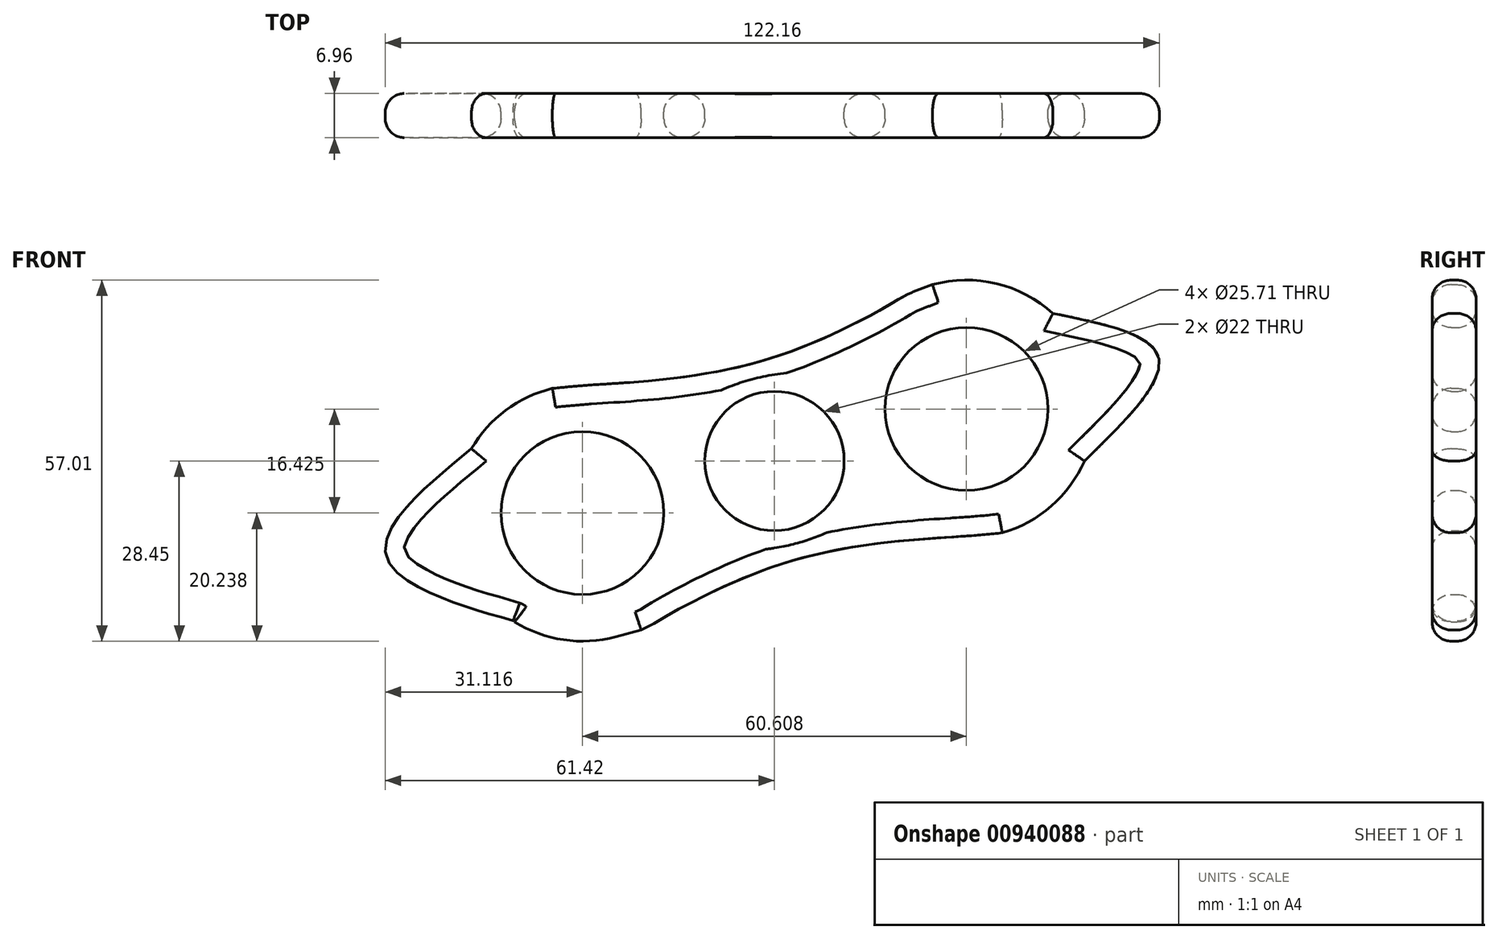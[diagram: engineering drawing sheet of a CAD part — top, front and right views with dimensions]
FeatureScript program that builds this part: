
annotation { "Feature Type Name" : "Feature", "Feature Type Description" : "" }
export const myFeature = defineFeature(function(context is Context, id is Id, definition is map)
    precondition{}
    {
        {
            var Q0;
            Q0=qCreatedBy(makeId("Front.planeOp"),FACE);
            var sketch = newSketch(context, id + "F0", { "sketchPlane" : qUnion([Q0])});
            skCircle(sketch, "E0", {"center": v(0, 0) * mm, "radius": 11 * mm});
            skPoint(sketch, "E1.0.midPoint", {"position": v(38.52, -22.1) * mm});
            skLineSegment(sketch, "E2", {"start": v(10.62, 2.88) * mm, "end": v(10.66, 2.89) * mm});
            skLineSegment(sketch, "E3", {"start": v(-10.62, -2.88) * mm, "end": v(-10.77, -2.92) * mm});
            skCircle(sketch, "E4", {"center": v(30.3, 8.21) * mm, "radius": 12.86 * mm});
            skCircle(sketch, "E5", {"center": v(-30.3, -8.21) * mm, "radius": 12.86 * mm});
            skArc(sketch, "E6", {"start": v(-42.6, -24.29) * mm, "mid": v(-34.23, -28.07) * mm, "end": v(-25.04, -27.75) * mm});
            skArc(sketch, "E7", {"start": v(43.95, 23.3) * mm, "mid": v(32.98, 28.38) * mm, "end": v(21.06, 26.34) * mm});
            skLineSegment(sketch, "E8", {"start": v(35.96, -11.34) * mm, "end": v(35.23, -11.53) * mm});
            skFitSpline(sketch, "E9", {"points": [v(-35.04, 11.46) * mm, v(-29.1, 11.99) * mm, v(-1.76, 15.86) * mm, v(19.32, 25.34) * mm, v(21.06, 26.34) * mm, v(24.94, 27.84) * mm], "startDerivative": vector(31.45, 3.25) * mm, "endDerivative": vector(35.22, 13.02) * mm});
            skFitSpline(sketch, "E10", {"points": [v(35.96, -11.34) * mm, v(30.02, -11.87) * mm, v(2.68, -15.78) * mm, v(-18.39, -25.29) * mm, v(-20.13, -26.29) * mm, v(-24, -27.8) * mm], "startDerivative": vector(-31.44, -3.3) * mm, "endDerivative": vector(-35.2, -13.06) * mm});
            skPoint(sketch, "E11.orphan", {"position": v(-16.42, 60.6) * mm});
            skPoint(sketch, "E12.orphan", {"position": v(16.42, -60.6) * mm});
            skPoint(sketch, "E13.orphan", {"position": v(60.6, 16.42) * mm});
            skLineSegment(sketch, "E14.trimOffspring", {"start": v(-21.04, -26.68) * mm, "end": v(-25.04, -27.75) * mm});
            skPoint(sketch, "E15.orphan", {"position": v(-60.6, -16.42) * mm});
            skLineSegment(sketch, "E16.trimOffspring", {"start": v(-30.05, -8.14) * mm, "end": v(-30.3, -8.21) * mm});
            skLineSegment(sketch, "E17.trimOffspring", {"start": v(30.3, 8.21) * mm, "end": v(30.45, 8.25) * mm});
            skLineSegment(sketch, "E18", {"start": v(-30.3, -8.21) * mm, "end": v(-30.05, -8.14) * mm});
            skLineSegment(sketch, "E19", {"start": v(-48.8, 0) * mm, "end": v(-48.8, 0) * mm});
            skFitSpline(sketch, "E20", {"points": [v(43.95, 23.3) * mm, v(60.6, 16.42) * mm, v(48.92, 0) * mm], "startDerivative": vector(48.13, -9.83) * mm, "endDerivative": vector(-37.39, -36.53) * mm});
            skArc(sketch, "E21.trimOffspring", {"start": v(-29.1, 11.99) * mm, "mid": v(-39.88, 9.61) * mm, "end": v(-47.81, 1.93) * mm});
            skLineSegment(sketch, "E22.trimOffspring", {"start": v(-10.77, -2.92) * mm, "end": v(-10.62, -2.88) * mm});
            skArc(sketch, "E23.trimOffspring", {"start": v(27.98, -12) * mm, "mid": v(40.42, -9.44) * mm, "end": v(48.92, 0) * mm});
            skFitSpline(sketch, "E24", {"points": [v(-47.81, 1.93) * mm, v(-60.6, -16.42) * mm, v(-41.26, -25.23) * mm, v(-41.02, -25.38) * mm], "startDerivative": vector(-50.87, -41.8) * mm, "endDerivative": vector(1.15, -2.34) * mm});
            skSolve(sketch);
        }
        {
            var Q0;
            Q0=makeQuery(id+"F0.imprint","IMPRINT",FACE,{"disambiguationData":[TD([[makeQuery(id+"F0.imprint","IMPRINT",EDGE,{"derivedFrom":sQuery(id+"F0.wireOp",EDGE,"E4")}),-1.0]])]});
            extrude(context, id + "F1", {"entities" : qUnion([Q0]), "depth" : 6.96 * mm, "offsetDistance" : 25 * mm});
        }
        {
            var Q0;
            Q0=makeQuery(id+"F1.opExtrude","CAP_FACE",FACE,{"disambiguationData":[OSD([sQuery(id+"F0.wireOp",EDGE,"E0"),sQuery(id+"F0.wireOp",EDGE,"E4"),sQuery(id+"F0.wireOp",EDGE,"E5"),sQuery(id+"F0.wireOp",EDGE,"E6"),sQuery(id+"F0.wireOp",EDGE,"E7"),sQuery(id+"F0.wireOp",EDGE,"E9"),sQuery(id+"F0.wireOp",EDGE,"E10"),sQuery(id+"F0.wireOp",EDGE,"E14.trimOffspring"),sQuery(id+"F0.wireOp",EDGE,"E20"),sQuery(id+"F0.wireOp",EDGE,"E21.trimOffspring"),sQuery(id+"F0.wireOp",EDGE,"E23.trimOffspring"),sQuery(id+"F0.wireOp",EDGE,"E24")])],"isStart":false});
            var Q1;
            Q1=makeQuery(id+"F1.opExtrude","CAP_FACE",FACE,{"disambiguationData":[OSD([sQuery(id+"F0.wireOp",EDGE,"E0"),sQuery(id+"F0.wireOp",EDGE,"E4"),sQuery(id+"F0.wireOp",EDGE,"E5"),sQuery(id+"F0.wireOp",EDGE,"E6"),sQuery(id+"F0.wireOp",EDGE,"E7"),sQuery(id+"F0.wireOp",EDGE,"E9"),sQuery(id+"F0.wireOp",EDGE,"E10"),sQuery(id+"F0.wireOp",EDGE,"E14.trimOffspring"),sQuery(id+"F0.wireOp",EDGE,"E20"),sQuery(id+"F0.wireOp",EDGE,"E21.trimOffspring"),sQuery(id+"F0.wireOp",EDGE,"E23.trimOffspring"),sQuery(id+"F0.wireOp",EDGE,"E24")])],"isStart":true});
            fillet(context, id + "F2", {"entities" : qUnion([Q0, Q1]), "radius" : 3 * mm, "tangentPropagation" : true, "allowEdgeOverflow" : false});
        }
    });
